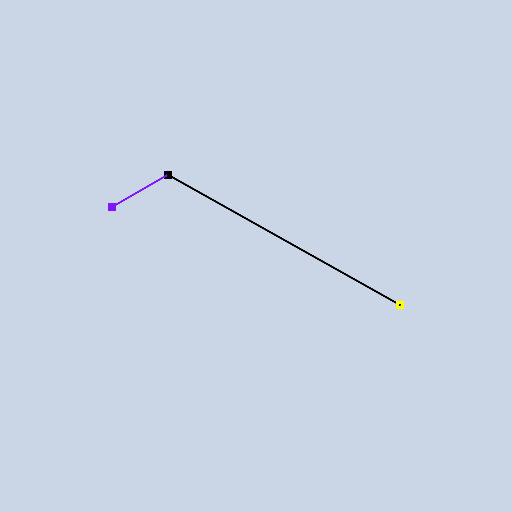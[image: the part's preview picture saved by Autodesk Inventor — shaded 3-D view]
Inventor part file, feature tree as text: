
AUTODESK INVENTOR PART (.ipt)
format: ipt  version: 2025 (Build 290162000, 162)  size: 92,160 bytes
history: native  units: in
note: dims shown in document units (in); Inventor stores cm internally (conversion verified against a paired STEP export)
features: other x2, plane x1, sketch x1
ambient origin geometry x8: Origin, YZ Plane, XZ Plane, XY Plane, X Axis, Y Axis, Z Axis, Center Point
feature tree (4):
  other  "Work Point1"
  other  "Work Point2"
  plane  "Work Plane1"
  sketch  "3D Sketch1"
